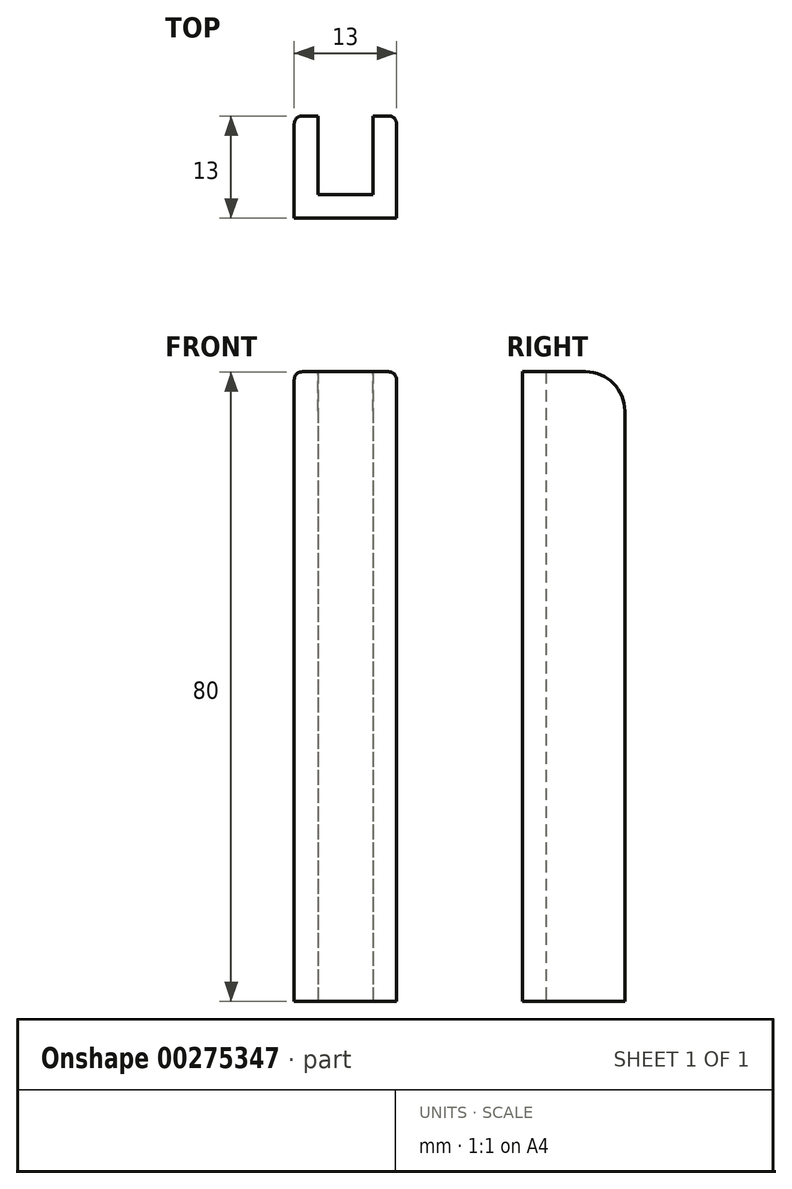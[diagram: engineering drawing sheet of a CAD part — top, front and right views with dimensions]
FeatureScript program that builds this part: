
annotation { "Feature Type Name" : "Feature", "Feature Type Description" : "" }
export const myFeature = defineFeature(function(context is Context, id is Id, definition is map)
    precondition{}
    {
        {
            var Q0;
            Q0=qCreatedBy(makeId("Right.planeOp"),FACE);
            var sketch = newSketch(context, id + "F0", { "sketchPlane" : qUnion([Q0])});
            skLineSegment(sketch, "E0", {"start": v(-69.88, 19.14) * mm, "end": v(-69.88, -60.86) * mm});
            skLineSegment(sketch, "E1", {"start": v(-69.88, 19.14) * mm, "end": v(-56.88, 19.14) * mm});
            skLineSegment(sketch, "E2", {"start": v(-56.88, 19.14) * mm, "end": v(-56.88, -47.86) * mm});
            skLineSegment(sketch, "E3", {"start": v(-56.88, -47.86) * mm, "end": v(-56.88, -60.86) * mm});
            skLineSegment(sketch, "E4", {"start": v(-69.88, -60.86) * mm, "end": v(-56.88, -60.86) * mm});
            skSolve(sketch);
        }
        {
            var Q0;
            Q0 = qSketchRegion(id + "F0", true);
            extrude(context, id + "F1", {"entities" : qUnion([Q0]), "depth" : 13 * mm});
        }
        {
            var Q0;
            {var subQ0=sQuery(id+"F0.wireOp",EDGE,"E2");var subQ1=sQuery(id+"F0.wireOp",EDGE,"E1");Q0=makeQuery(id+"FJcnYLYFH9kqATZ_1.boolean.opBoolean","SPLIT",EDGE,{"disambiguationData":[TD([makeQuery(id+"FJcnYLYFH9kqATZ_1.opExtrude","SWEPT_FACE",FACE,{"disambiguationData":[OSD([sQuery(id+"FENz25jsiHndIak_1.wireOp",EDGE,"mASXkQR2-8rtL-BK8H-pKuD-AHrAa0D44IAr.right")])]})])],"derivedFrom":makeQuery(id+"F1.opExtrude","SWEPT_EDGE",EDGE,{"disambiguationData":[OSD([subQ1,subQ0])]})});}
            var Q1;
            {var subQ0=sQuery(id+"F0.wireOp",EDGE,"E2");var subQ1=sQuery(id+"F0.wireOp",EDGE,"E1");Q1=makeQuery(id+"FJcnYLYFH9kqATZ_1.boolean.opBoolean","SPLIT",EDGE,{"disambiguationData":[TD([makeQuery(id+"FJcnYLYFH9kqATZ_1.opExtrude","SWEPT_FACE",FACE,{"disambiguationData":[OSD([sQuery(id+"FENz25jsiHndIak_1.wireOp",EDGE,"mASXkQR2-8rtL-BK8H-pKuD-AHrAa0D44IAr.left")])]})])],"derivedFrom":makeQuery(id+"F1.opExtrude","SWEPT_EDGE",EDGE,{"disambiguationData":[OSD([subQ1,subQ0])]})});}
            var Q2;
            {var subQ0=sQuery(id+"F0.wireOp",EDGE,"zP6Eez7k-3vkM-WNZK-C4u4-quo0aUFXeNZ8");var subQ1=sQuery(id+"F0.wireOp",EDGE,"yq7QDu4M-jQ4w-5Hrm-DH4a-3fNfTdXy6jlA");Q2=makeQuery(id+"FJcnYLYFH9kqATZ_1.boolean.opBoolean","SPLIT",EDGE,{"disambiguationData":[TD([makeQuery(id+"FJcnYLYFH9kqATZ_1.opExtrude","SWEPT_FACE",FACE,{"disambiguationData":[OSD([sQuery(id+"FENz25jsiHndIak_1.wireOp",EDGE,"mASXkQR2-8rtL-BK8H-pKuD-AHrAa0D44IAr.right")])]})])],"derivedFrom":makeQuery(id+"F1.opExtrude","SWEPT_EDGE",EDGE,{"disambiguationData":[OSD([subQ1,subQ0])]})});}
            var Q3;
            {var subQ0=sQuery(id+"F0.wireOp",EDGE,"zP6Eez7k-3vkM-WNZK-C4u4-quo0aUFXeNZ8");var subQ1=sQuery(id+"F0.wireOp",EDGE,"yq7QDu4M-jQ4w-5Hrm-DH4a-3fNfTdXy6jlA");Q3=makeQuery(id+"FJcnYLYFH9kqATZ_1.boolean.opBoolean","SPLIT",EDGE,{"disambiguationData":[TD([makeQuery(id+"FJcnYLYFH9kqATZ_1.opExtrude","SWEPT_FACE",FACE,{"disambiguationData":[OSD([sQuery(id+"FENz25jsiHndIak_1.wireOp",EDGE,"mASXkQR2-8rtL-BK8H-pKuD-AHrAa0D44IAr.left")])]})])],"derivedFrom":makeQuery(id+"F1.opExtrude","SWEPT_EDGE",EDGE,{"disambiguationData":[OSD([subQ1,subQ0])]})});}
            var Q4;
            {var subQ0=sQuery(id+"F0.wireOp",EDGE,"yq7QDu4M-jQ4w-5Hrm-DH4a-3fNfTdXy6jlA");var subQ1=sQuery(id+"F0.wireOp",EDGE,"E2");Q4=makeQuery(id+"FJcnYLYFH9kqATZ_1.boolean.opBoolean","SPLIT",EDGE,{"disambiguationData":[TD([makeQuery(id+"FJcnYLYFH9kqATZ_1.opExtrude","SWEPT_FACE",FACE,{"disambiguationData":[OSD([sQuery(id+"FENz25jsiHndIak_1.wireOp",EDGE,"mASXkQR2-8rtL-BK8H-pKuD-AHrAa0D44IAr.left")])]})])],"derivedFrom":makeQuery(id+"F1.opExtrude","SWEPT_EDGE",EDGE,{"disambiguationData":[OSD([subQ1,subQ0])]})});}
            var Q5;
            {var subQ0=sQuery(id+"F0.wireOp",EDGE,"yq7QDu4M-jQ4w-5Hrm-DH4a-3fNfTdXy6jlA");var subQ1=sQuery(id+"F0.wireOp",EDGE,"E2");Q5=makeQuery(id+"FJcnYLYFH9kqATZ_1.boolean.opBoolean","SPLIT",EDGE,{"disambiguationData":[TD([makeQuery(id+"FJcnYLYFH9kqATZ_1.opExtrude","SWEPT_FACE",FACE,{"disambiguationData":[OSD([sQuery(id+"FENz25jsiHndIak_1.wireOp",EDGE,"mASXkQR2-8rtL-BK8H-pKuD-AHrAa0D44IAr.right")])]})])],"derivedFrom":makeQuery(id+"F1.opExtrude","SWEPT_EDGE",EDGE,{"disambiguationData":[OSD([subQ1,subQ0])]})});}
            fillet(context, id + "F2", {"entities" : qUnion([Q0, Q1, Q2, Q3, Q4, Q5]), "radius" : 5 * mm, "tangentPropagation" : true, "allowEdgeOverflow" : false});
        }
        {
            var Q0;
            Q0=makeQuery(id+"F1.opExtrude","CAP_EDGE",EDGE,{"disambiguationData":[OSD([sQuery(id+"F0.wireOp",EDGE,"E2")])],"isStart":true});
            var Q1;
            Q1=makeQuery(id+"F1.opExtrude","CAP_EDGE",EDGE,{"disambiguationData":[OSD([sQuery(id+"F0.wireOp",EDGE,"E2")])],"isStart":false});
            var Q2;
            Q2=makeQuery(id+"FJcnYLYFH9kqATZ_1.boolean.opBoolean","INTERSECT",EDGE,{"derivedFrom":[makeQuery(id+"F1.opExtrude","SWEPT_FACE",FACE,{"disambiguationData":[OSD([sQuery(id+"F0.wireOp",EDGE,"E1")])]}),makeQuery(id+"FJcnYLYFH9kqATZ_1.opExtrude","CAP_FACE",FACE,{"disambiguationData":[OSD([sQuery(id+"FENz25jsiHndIak_1.wireOp",EDGE,"mASXkQR2-8rtL-BK8H-pKuD-AHrAa0D44IAr.bottom"),sQuery(id+"FENz25jsiHndIak_1.wireOp",EDGE,"mASXkQR2-8rtL-BK8H-pKuD-AHrAa0D44IAr.top"),sQuery(id+"FENz25jsiHndIak_1.wireOp",EDGE,"mASXkQR2-8rtL-BK8H-pKuD-AHrAa0D44IAr.left"),sQuery(id+"FENz25jsiHndIak_1.wireOp",EDGE,"mASXkQR2-8rtL-BK8H-pKuD-AHrAa0D44IAr.right")])],"isStart":false})]});
            var Q3;
            Q3=makeQuery(id+"FJcnYLYFH9kqATZ_1.boolean.opBoolean","COPY",EDGE,{"derivedFrom":makeQuery(id+"FJcnYLYFH9kqATZ_1.opExtrude","CAP_EDGE",EDGE,{"disambiguationData":[OSD([sQuery(id+"FENz25jsiHndIak_1.wireOp",EDGE,"mASXkQR2-8rtL-BK8H-pKuD-AHrAa0D44IAr.top")])],"isStart":true})});
            fillet(context, id + "F3", {"entities" : qUnion([Q0, Q1, Q2, Q3]), "radius" : 1 * mm, "tangentPropagation" : true, "allowEdgeOverflow" : false});
        }
        {
            var Q0;
            Q0=makeQuery(id+"F1.opExtrude","SWEPT_FACE",FACE,{"disambiguationData":[OSD([sQuery(id+"F0.wireOp",EDGE,"E2"),sQuery(id+"F0.wireOp",EDGE,"E3")])]});
            var sketch = newSketch(context, id + "F4", { "sketchPlane" : qUnion([Q0])});
            skLineSegment(sketch, "E5.bottom", {"start": v(-10, 19.2) * mm, "end": v(-3, 19.2) * mm});
            skLineSegment(sketch, "E5.top", {"start": v(-10, -60.86) * mm, "end": v(-3, -60.86) * mm});
            skLineSegment(sketch, "E5.left", {"start": v(-10, 19.2) * mm, "end": v(-10, -60.86) * mm});
            skLineSegment(sketch, "E5.right", {"start": v(-3, 19.2) * mm, "end": v(-3, -60.86) * mm});
            skSolve(sketch);
        }
        {
            var Q0;
            Q0 = qSketchRegion(id + "F4", true);
            extrude(context, id + "F5", {"entities" : qUnion([Q0]), "operationType" : NewBodyOperationType.REMOVE, "oppositeDirection" : true, "depth" : 10 * mm});
        }
    });
